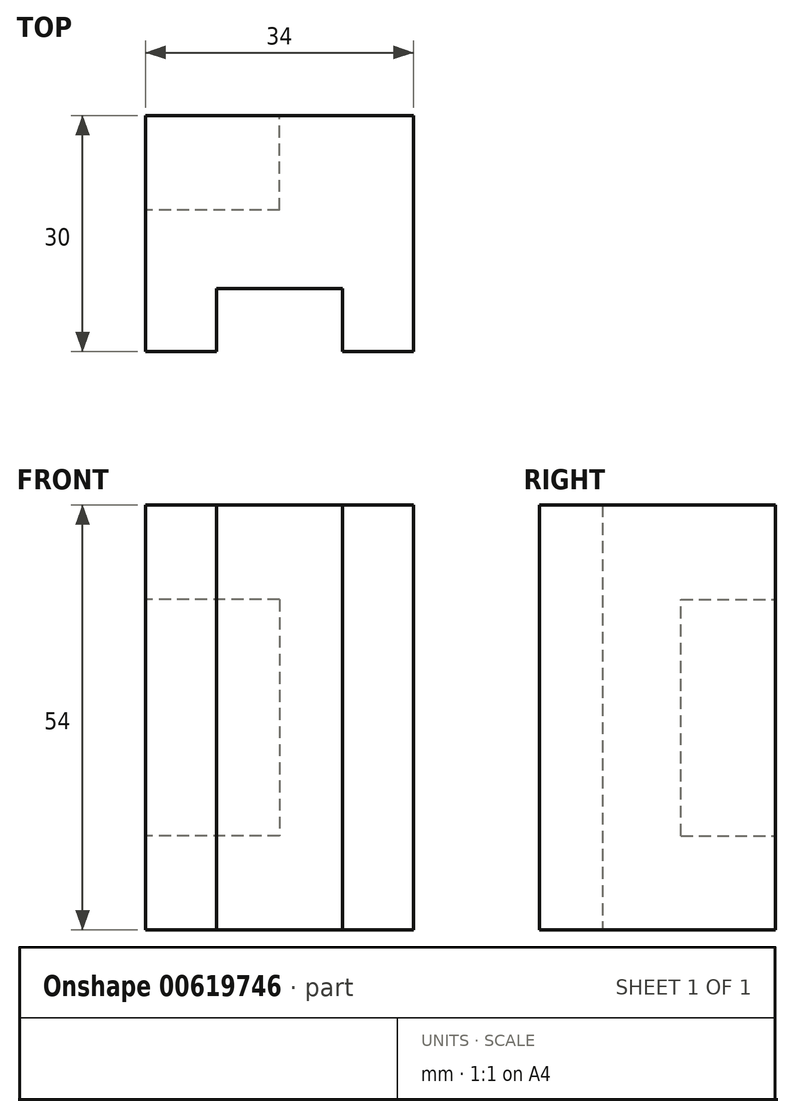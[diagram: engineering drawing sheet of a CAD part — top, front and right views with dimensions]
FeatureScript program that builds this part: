
annotation { "Feature Type Name" : "Feature", "Feature Type Description" : "" }
export const myFeature = defineFeature(function(context is Context, id is Id, definition is map)
    precondition{}
    {
        {
            var Q0;
            Q0=qCreatedBy(makeId("Top.planeOp"),FACE);
            var sketch = newSketch(context, id + "F0", { "sketchPlane" : qUnion([Q0])});
            skLineSegment(sketch, "E0.bottom", {"start": v(-17, 15) * mm, "end": v(17, 15) * mm});
            skLineSegment(sketch, "E0.top", {"start": v(-17, -15) * mm, "end": v(17, -15) * mm});
            skLineSegment(sketch, "E0.left", {"start": v(-17, 15) * mm, "end": v(-17, -15) * mm});
            skLineSegment(sketch, "E0.right", {"start": v(17, 15) * mm, "end": v(17, -15) * mm});
            skPoint(sketch, "E0.middle", {"position": v(0, 0) * mm});
            skLineSegment(sketch, "E1", {"start": v(0, 0) * mm, "end": v(0, 35.9) * mm, "construction": true});
            skLineSegment(sketch, "E2", {"start": v(0, 0) * mm, "end": v(0, -33.05) * mm});
            skLineSegment(sketch, "E3.left", {"start": v(-8, -7) * mm, "end": v(-8, -15) * mm});
            skPoint(sketch, "E3.middle", {"position": v(-17, -15) * mm});
            skPoint(sketch, "E3.right.start.orphan", {"position": v(-26, -7) * mm});
            skPoint(sketch, "E3.top.end.orphan", {"position": v(-26, -23) * mm});
            skPoint(sketch, "E4.orphan", {"position": v(-8, -23) * mm});
            skLineSegment(sketch, "E5.left", {"start": v(8, -7) * mm, "end": v(8, -15) * mm});
            skPoint(sketch, "E5.middle", {"position": v(17, -15) * mm});
            skPoint(sketch, "E5.right.start.orphan", {"position": v(26, -7.98) * mm});
            skPoint(sketch, "E5.top.end.orphan", {"position": v(26, -23) * mm});
            skPoint(sketch, "E6.orphan", {"position": v(8, -22.02) * mm});
            skLineSegment(sketch, "E7", {"start": v(-8, -7) * mm, "end": v(8, -7) * mm});
            skSolve(sketch);
        }
        {
            var Q0;
            Q0=makeQuery(id+"F0.imprint","IMPRINT",FACE,{"disambiguationData":[TD([[makeQuery(id+"F0.imprint","IMPRINT",EDGE,{"derivedFrom":sQuery(id+"F0.wireOp",EDGE,"E0.bottom")}),-1.0]])]});
            extrude(context, id + "F1", {"entities" : qUnion([Q0]), "depth" : 54 * mm, "offsetDistance" : 25 * mm});
        }
        {
            var Q0;
            Q0=makeQuery(id+"F1.opExtrude","SWEPT_FACE",FACE,{"disambiguationData":[OSD([sQuery(id+"F0.wireOp",EDGE,"E0.left")])]});
            var sketch = newSketch(context, id + "F2", { "sketchPlane" : qUnion([Q0])});
            skLineSegment(sketch, "E8.bottom", {"start": v(-3, 12) * mm, "end": v(-15, 12) * mm});
            skLineSegment(sketch, "E8.top", {"start": v(-3, 42) * mm, "end": v(-15, 42) * mm});
            skLineSegment(sketch, "E8.left", {"start": v(-3, 12) * mm, "end": v(-3, 42) * mm});
            skLineSegment(sketch, "E8.right", {"start": v(-15, 12) * mm, "end": v(-15, 42) * mm});
            skPoint(sketch, "E8.middle", {"position": v(-9, 27) * mm});
            skSolve(sketch);
        }
        {
            var Q0;
            Q0=makeQuery(id+"F2.imprint","IMPRINT",FACE,{"disambiguationData":[TD([[makeQuery(id+"F2.imprint","IMPRINT",EDGE,{"derivedFrom":sQuery(id+"F2.wireOp",EDGE,"E8.bottom")}),-1.0]])]});
            extrude(context, id + "F3", {"entities" : qUnion([Q0]), "operationType" : NewBodyOperationType.REMOVE, "oppositeDirection" : true, "depth" : 17 * mm, "offsetDistance" : 25 * mm});
        }
    });
